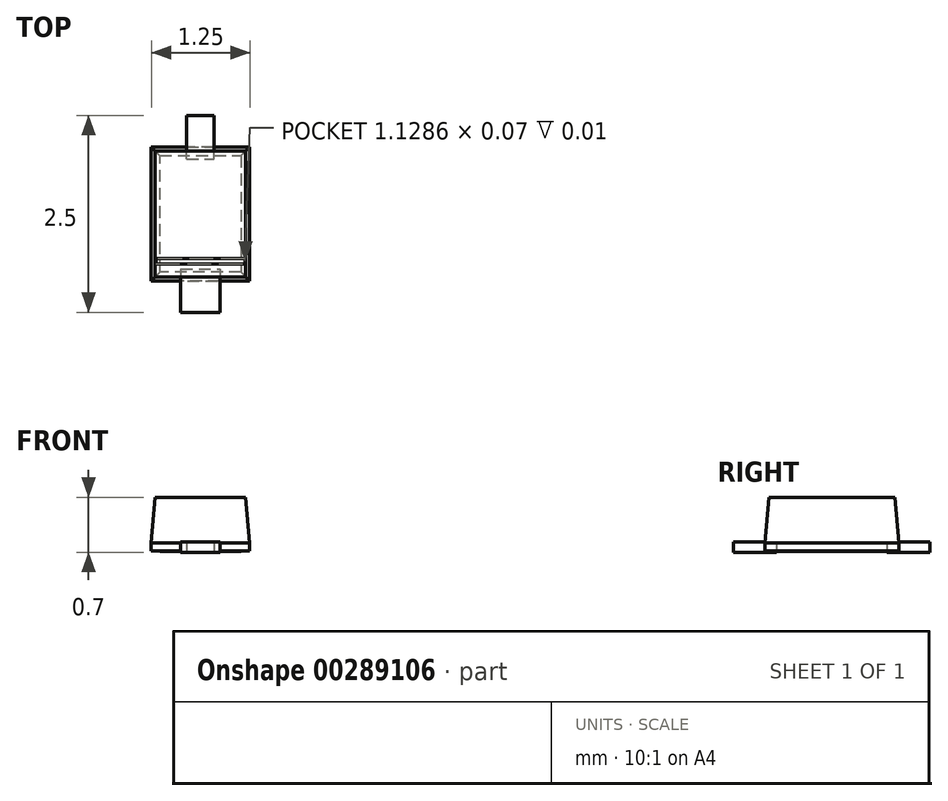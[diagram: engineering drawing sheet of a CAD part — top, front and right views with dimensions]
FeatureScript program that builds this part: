
annotation { "Feature Type Name" : "Feature", "Feature Type Description" : "" }
export const myFeature = defineFeature(function(context is Context, id is Id, definition is map)
    precondition{}
    {
        {
            var Q0;
            Q0=qCreatedBy(makeId("Top.planeOp"),FACE);
            var sketch = newSketch(context, id + "F0", { "sketchPlane" : qUnion([Q0])});
            skLineSegment(sketch, "E0.bottom", {"start": v(-0.25, -0.7) * mm, "end": v(0.25, -0.7) * mm});
            skLineSegment(sketch, "E0.top", {"start": v(-0.25, -1.25) * mm, "end": v(0.25, -1.25) * mm});
            skLineSegment(sketch, "E0.left", {"start": v(-0.25, -0.7) * mm, "end": v(-0.25, -1.25) * mm});
            skLineSegment(sketch, "E0.right", {"start": v(0.25, -0.7) * mm, "end": v(0.25, -1.25) * mm});
            skPoint(sketch, "E0.middle", {"position": v(0, -0.98) * mm});
            skLineSegment(sketch, "E1.bottom", {"start": v(-0.17, 0.7) * mm, "end": v(0.18, 0.7) * mm});
            skLineSegment(sketch, "E1.top", {"start": v(-0.17, 1.25) * mm, "end": v(0.18, 1.25) * mm});
            skLineSegment(sketch, "E1.left", {"start": v(-0.17, 0.7) * mm, "end": v(-0.17, 1.25) * mm});
            skLineSegment(sketch, "E1.right", {"start": v(0.18, 0.7) * mm, "end": v(0.18, 1.25) * mm});
            skPoint(sketch, "E1.middle", {"position": v(0, 0.98) * mm});
            skLineSegment(sketch, "E2", {"start": v(0, 0.98) * mm, "end": v(0, -0.98) * mm, "construction": true});
            skPoint(sketch, "E3", {"position": v(0, 0) * mm});
            skSolve(sketch);
        }
        {
            var Q0;
            Q0 = qSketchRegion(id + "F0", true);
            extrude(context, id + "F1", {"entities" : qUnion([Q0]), "depth" : 0.13 * mm, "offsetDistance" : 25 * mm});
        }
        {
            var Q0;
            Q0=qCreatedBy(makeId("Top.planeOp"),FACE);
            cPlane(context, id + "F2", {"entities" : qUnion([Q0]), "cplaneType" : CPlaneType.OFFSET, "offset" : 0.12 * mm, "width" : 150 * mm, "height" : 150 * mm});
        }
        {
            var Q0;
            Q0=qCreatedBy(id+"F2.planeOp",FACE);
            var sketch = newSketch(context, id + "F3", { "sketchPlane" : qUnion([Q0])});
            skLineSegment(sketch, "E4.bottom", {"start": v(0.62, -0.85) * mm, "end": v(-0.63, -0.85) * mm});
            skLineSegment(sketch, "E4.top", {"start": v(0.62, 0.85) * mm, "end": v(-0.62, 0.85) * mm});
            skLineSegment(sketch, "E4.left", {"start": v(0.62, -0.85) * mm, "end": v(0.62, 0.85) * mm});
            skLineSegment(sketch, "E4.right", {"start": v(-0.63, -0.85) * mm, "end": v(-0.62, 0.85) * mm});
            skPoint(sketch, "E4.middle", {"position": v(0, 0) * mm});
            skSolve(sketch);
        }
        {
            var Q0;
            Q0 = qSketchRegion(id + "F3", true);
            extrude(context, id + "F4", {"entities" : qUnion([Q0]), "depth" : (0.7 - 0.12) * mm, "offsetDistance" : 25 * mm, "hasSecondDirection" : true, "secondDirectionOppositeDirection" : true, "secondDirectionDepth" : 0.1 * mm});
        }
        {
            var Q0;
            Q0=makeQuery(id+"F4.opExtrude","CAP_FACE",FACE,{"disambiguationData":[OSD([sQuery(id+"F3.wireOp",EDGE,"E4.bottom"),sQuery(id+"F3.wireOp",EDGE,"E4.top"),sQuery(id+"F3.wireOp",EDGE,"E4.left"),sQuery(id+"F3.wireOp",EDGE,"E4.right")])],"isStart":false});
            chamfer(context, id + "F5", {"entities" : qUnion([Q0]), "chamferType" : ChamferType.OFFSET_ANGLE, "width" : 0.58 * mm, "oppositeDirection" : false, "angle" : 5 * degree, "tangentPropagation" : true});
        }
        {
            var Q0;
            Q0=makeQuery(id+"F4.opExtrude","CAP_EDGE",EDGE,{"disambiguationData":[OSD([sQuery(id+"F3.wireOp",EDGE,"E4.left")])],"isStart":true});
            var Q1;
            Q1=makeQuery(id+"F4.opExtrude","CAP_EDGE",EDGE,{"disambiguationData":[OSD([sQuery(id+"F3.wireOp",EDGE,"E4.top")])],"isStart":true});
            var Q2;
            Q2=makeQuery(id+"F4.opExtrude","CAP_EDGE",EDGE,{"disambiguationData":[OSD([sQuery(id+"F3.wireOp",EDGE,"E4.right")])],"isStart":true});
            var Q3;
            Q3=makeQuery(id+"F4.opExtrude","CAP_EDGE",EDGE,{"disambiguationData":[OSD([sQuery(id+"F3.wireOp",EDGE,"E4.bottom")])],"isStart":true});
            chamfer(context, id + "F6", {"entities" : qUnion([Q0, Q1, Q2, Q3]), "chamferType" : ChamferType.OFFSET_ANGLE, "width" : 0.1 * mm, "oppositeDirection" : false, "angle" : 5 * degree, "tangentPropagation" : true});
        }
        {
            var Q0;
            Q0=makeQuery(id+"F4.opExtrude","CAP_FACE",FACE,{"disambiguationData":[OSD([sQuery(id+"F3.wireOp",EDGE,"E4.bottom"),sQuery(id+"F3.wireOp",EDGE,"E4.top"),sQuery(id+"F3.wireOp",EDGE,"E4.left"),sQuery(id+"F3.wireOp",EDGE,"E4.right")])],"isStart":false});
            var sketch = newSketch(context, id + "F7", { "sketchPlane" : qUnion([Q0])});
            skLineSegment(sketch, "E5.bottom", {"start": v(0.56, -0.63) * mm, "end": v(-0.56, -0.63) * mm});
            skLineSegment(sketch, "E5.top", {"start": v(0.56, -0.56) * mm, "end": v(-0.56, -0.56) * mm});
            skLineSegment(sketch, "E5.left", {"start": v(0.56, -0.63) * mm, "end": v(0.56, -0.56) * mm});
            skLineSegment(sketch, "E5.right", {"start": v(-0.56, -0.63) * mm, "end": v(-0.56, -0.56) * mm});
            skPoint(sketch, "E5.middle", {"position": v(0, -0.6) * mm});
            skSolve(sketch);
        }
        {
            var Q0;
            Q0 = qSketchRegion(id + "F7", true);
            extrude(context, id + "F8", {"entities" : qUnion([Q0]), "oppositeDirection" : true, "depth" : 0.01 * mm, "offsetDistance" : 25 * mm});
        }
        {
            var Q0;
            Q0=makeQuery(id+"F8.opExtrude","SWEPT_BODY",BODY,{"disambiguationData":[OSD([sQuery(id+"F7.wireOp",EDGE,"E5.bottom"),sQuery(id+"F7.wireOp",EDGE,"E5.top"),sQuery(id+"F7.wireOp",EDGE,"E5.left"),sQuery(id+"F7.wireOp",EDGE,"E5.right")])]});
            var Q1;
            Q1=makeQuery(id+"F4.opExtrude","SWEPT_BODY",BODY,{"disambiguationData":[OSD([sQuery(id+"F3.wireOp",EDGE,"E4.bottom"),sQuery(id+"F3.wireOp",EDGE,"E4.top"),sQuery(id+"F3.wireOp",EDGE,"E4.left"),sQuery(id+"F3.wireOp",EDGE,"E4.right")])]});
            booleanBodies(context, id + "F9", {"operationType" : BooleanOperationType.SUBTRACTION, "tools" : qUnion([Q0]), "targets" : qUnion([Q1]), "keepTools" : true});
        }
    });
